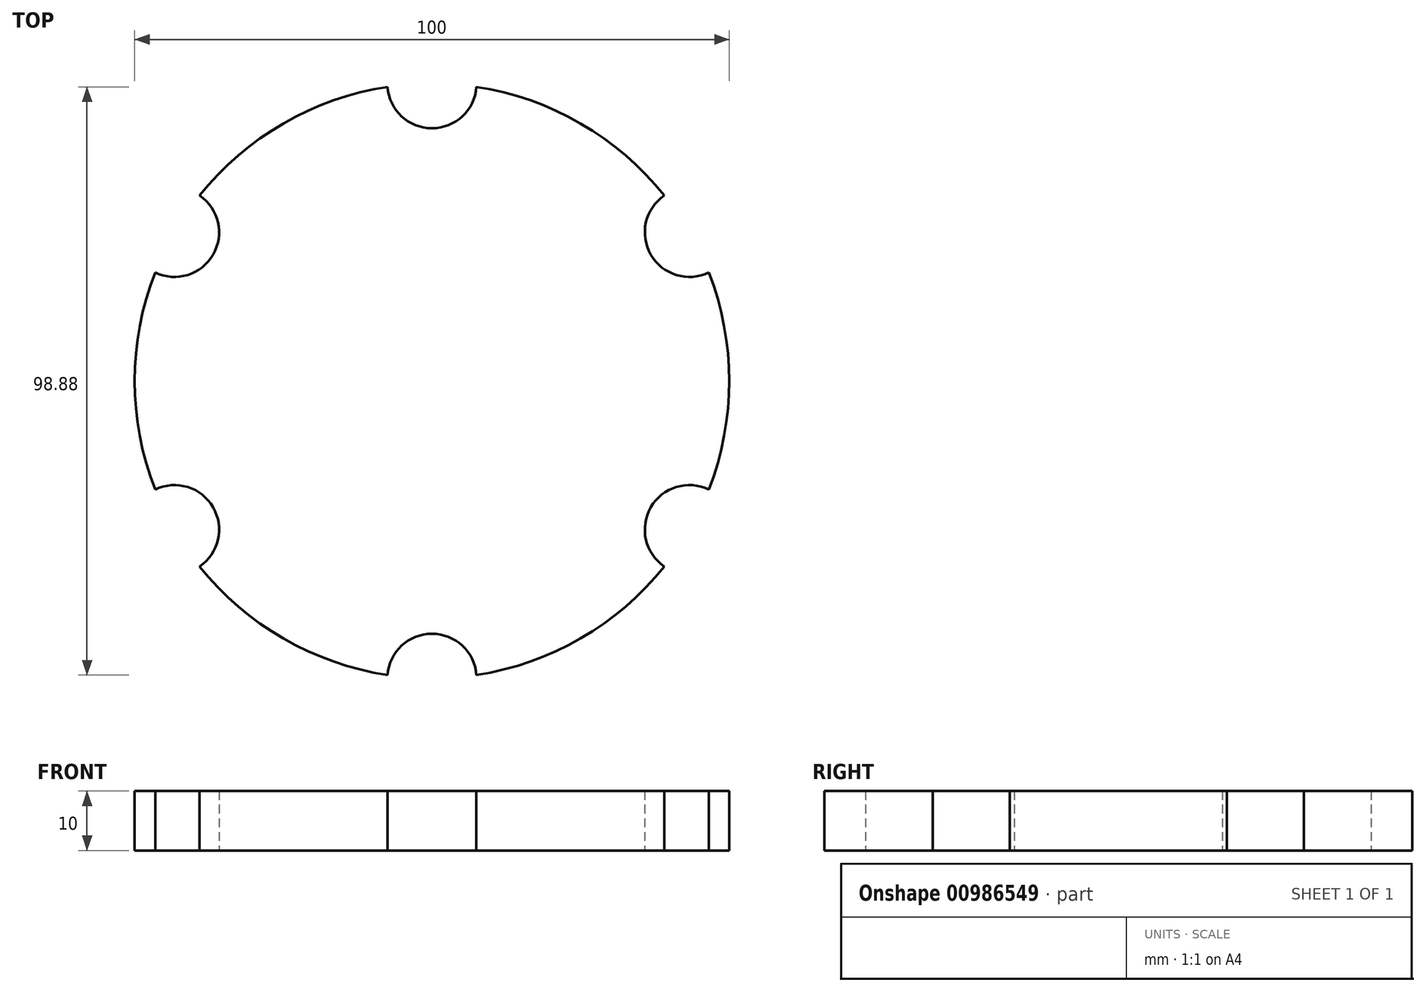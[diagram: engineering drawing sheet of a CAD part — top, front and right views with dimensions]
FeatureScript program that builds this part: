
annotation { "Feature Type Name" : "Feature", "Feature Type Description" : "" }
export const myFeature = defineFeature(function(context is Context, id is Id, definition is map)
    precondition{}
    {
        {
            var Q0;
            Q0=qCreatedBy(makeId("Top.planeOp"),FACE);
            var sketch = newSketch(context, id + "F0", { "sketchPlane" : qUnion([Q0])});
            skCircle(sketch, "E0", {"center": v(0, 0) * mm, "radius": 50 * mm});
            skCircle(sketch, "E1", {"center": v(0, 50) * mm, "radius": 7.5 * mm});
            skCircle(sketch, "E2", {"center": v(43.3, 25) * mm, "radius": 7.5 * mm});
            skCircle(sketch, "E3", {"center": v(43.3, -25) * mm, "radius": 7.5 * mm});
            skCircle(sketch, "E4", {"center": v(0, -50) * mm, "radius": 7.5 * mm});
            skCircle(sketch, "E5", {"center": v(-43.3, -25) * mm, "radius": 7.5 * mm});
            skCircle(sketch, "E6", {"center": v(-43.3, 25) * mm, "radius": 7.5 * mm});
            skSolve(sketch);
        }
        {
            var Q0;
            {var subQ1=sQuery(id+"F0.wireOp",EDGE,"E0");var subQ12=sQuery(id+"F0.wireOp",EDGE,"E6");var subQ13=makeQuery(id+"F0.imprint","INTERSECT",VERTEX,{"disambiguationData":[OD(0.0)],"derivedFrom":[subQ1,subQ12]});var subQ19=makeQuery(id+"F0.imprint","IMPRINT",FACE,{"disambiguationData":[TD([[makeQuery(id+"F0.imprint","IMPRINT",EDGE,{"disambiguationData":[TD([[subQ13,1.0]])],"derivedFrom":subQ1}),1.0]])]});Q0=qUnion([subQ19,subQ19,subQ19,subQ19,subQ19,subQ19]);}
            extrude(context, id + "F1", {"entities" : qUnion([Q0]), "depth" : 10 * mm});
        }
    });
